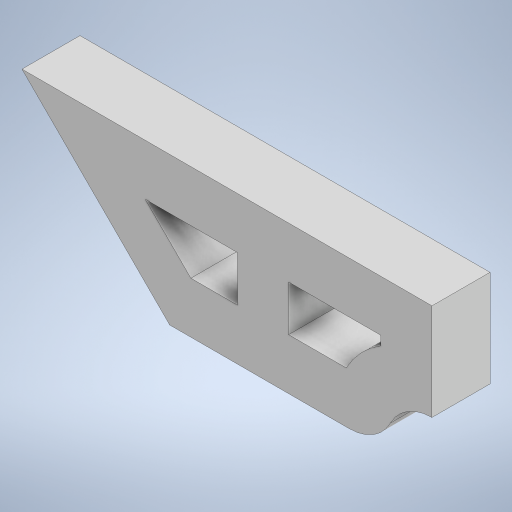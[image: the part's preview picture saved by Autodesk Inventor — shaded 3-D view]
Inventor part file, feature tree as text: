
AUTODESK INVENTOR PART (.ipt)
format: ipt  version: 2024 (Build 280153000, 153)  size: 253,440 bytes
history: native  units: in
note: dims shown in document units (in); Inventor stores cm internally (conversion verified against a paired STEP export)
features: extrude x2, sketch x2
ambient origin geometry x8: Origin, YZ Plane, XZ Plane, XY Plane, X Axis, Y Axis, Z Axis, Center Point
bodies: Solid1 (feature_tree)
feature tree (4):
  extrude  "Extrusion1"  Depth=0.44in
  extrude  "Extrusion2"  Depth=0.5in TaperAngle=0.0deg
  sketch  "Sketch1"  dims[d1=0.44in d2=0.44in]
  sketch  "Sketch2"  dims[d3=0.4in d4=0.5in d5=0.0in d6=2.7in d7=0.4in d9=1.8in d10=0.44in d11=0.22in d12=0.22in d13=0.5in d14=0.0in]
